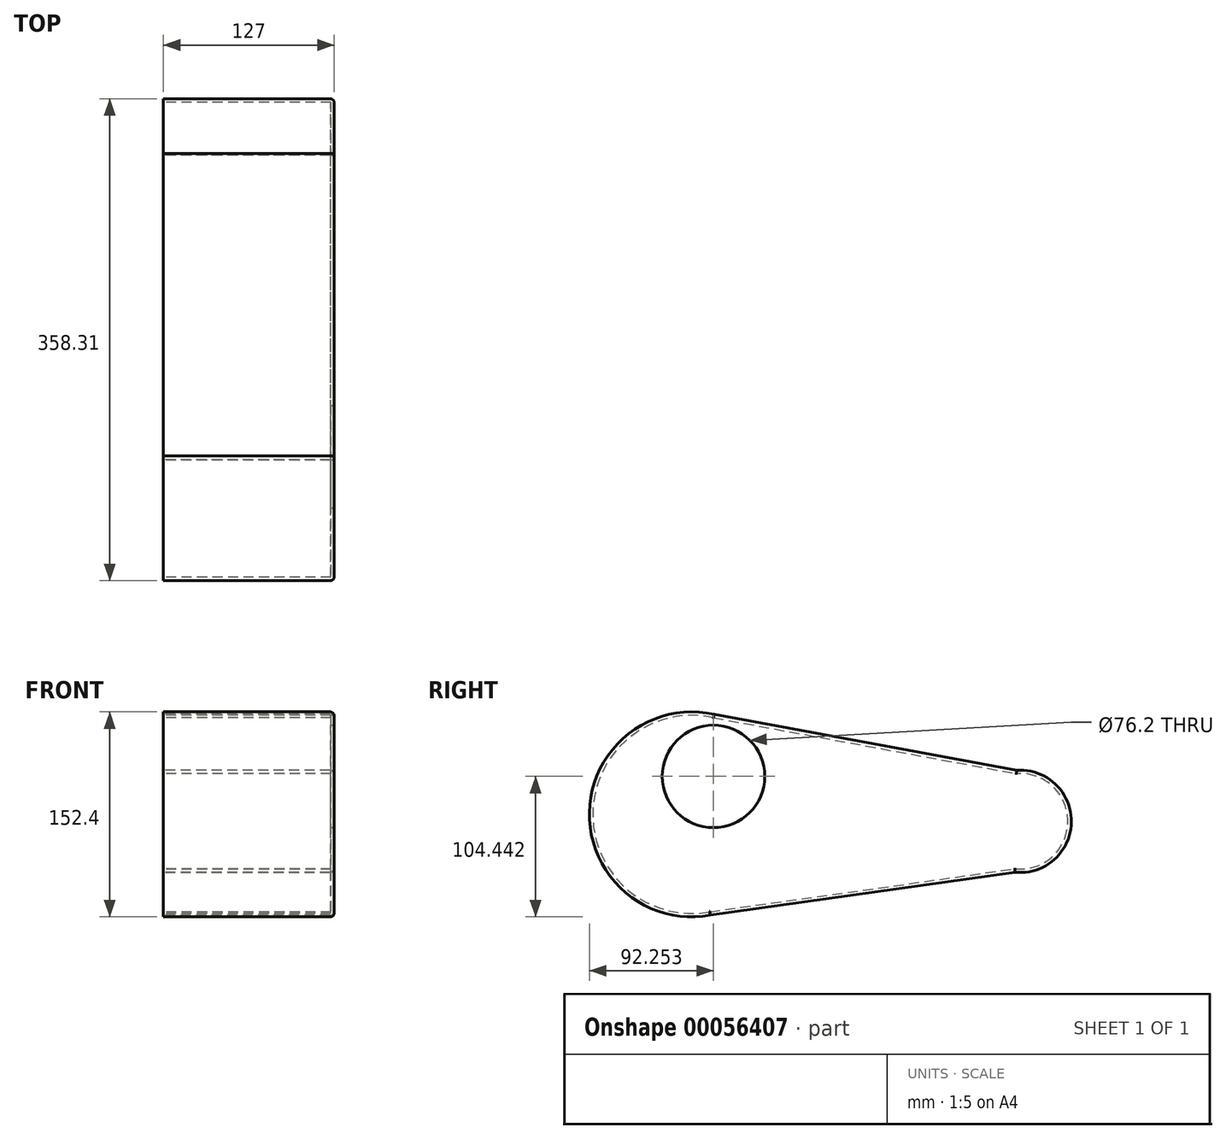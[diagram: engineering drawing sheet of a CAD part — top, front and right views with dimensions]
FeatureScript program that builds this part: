
annotation { "Feature Type Name" : "Feature", "Feature Type Description" : "" }
export const myFeature = defineFeature(function(context is Context, id is Id, definition is map)
    precondition{}
    {
        {
            var Q0;
            Q0=qCreatedBy(makeId("Right.planeOp"),FACE);
            var sketch = newSketch(context, id + "F0", { "sketchPlane" : qUnion([Q0])});
            skCircle(sketch, "E0", {"center": v(0, 0) * mm, "radius": 76.2 * mm});
            skCircle(sketch, "E1", {"center": v(244, -5.13) * mm, "radius": 38.1 * mm});
            skLineSegment(sketch, "E2", {"start": v(16.55, 74.38) * mm, "end": v(241.35, 32.88) * mm});
            skLineSegment(sketch, "E3", {"start": v(13.77, -74.95) * mm, "end": v(240.13, -43.03) * mm});
            skSolve(sketch);
        }
        {
            var Q0;
            {var subQ0=sQuery(id+"F0.wireOp",EDGE,"E0");var subQ1=makeQuery(id+"F0.imprint","INTERSECT",VERTEX,{"derivedFrom":[subQ0,sQuery(id+"F0.wireOp",EDGE,"E2")]});Q0=makeQuery(id+"F0.imprint","IMPRINT",FACE,{"disambiguationData":[TD([[makeQuery(id+"F0.imprint","IMPRINT",EDGE,{"disambiguationData":[TD([[subQ1,-1.0]])],"derivedFrom":subQ0}),1.0]])]});}
            var Q1;
            {var subQ0=sQuery(id+"F0.wireOp",EDGE,"E2");Q1=makeQuery(id+"F0.imprint","IMPRINT",FACE,{"disambiguationData":[TD([[makeQuery(id+"F0.imprint","IMPRINT",EDGE,{"derivedFrom":subQ0}),-1.0]])]});}
            var Q2;
            {var subQ0=sQuery(id+"F0.wireOp",EDGE,"E1");var subQ1=makeQuery(id+"F0.imprint","INTERSECT",VERTEX,{"derivedFrom":[subQ0,sQuery(id+"F0.wireOp",EDGE,"E2")]});Q2=makeQuery(id+"F0.imprint","IMPRINT",FACE,{"disambiguationData":[TD([[makeQuery(id+"F0.imprint","IMPRINT",EDGE,{"disambiguationData":[TD([[subQ1,-1.0]])],"derivedFrom":subQ0}),1.0]])]});}
            extrude(context, id + "F1", {"entities" : qUnion([Q0, Q1, Q2]), "depth" : 127 * mm});
        }
        {
            var Q0;
            Q0=makeQuery(id+"F1.opExtrude","CAP_FACE",FACE,{"disambiguationData":[OSD([sQuery(id+"F0.wireOp",EDGE,"E0"),sQuery(id+"F0.wireOp",EDGE,"E1"),sQuery(id+"F0.wireOp",EDGE,"E2"),sQuery(id+"F0.wireOp",EDGE,"E3")])],"isStart":false});
            var sketch = newSketch(context, id + "F2", { "sketchPlane" : qUnion([Q0])});
            skCircle(sketch, "E4", {"center": v(16.05, 28.24) * mm, "radius": 38.1 * mm});
            skSolve(sketch);
        }
        {
            var Q0;
            Q0=makeQuery(id+"F1.opExtrude","CAP_FACE",FACE,{"disambiguationData":[OSD([sQuery(id+"F0.wireOp",EDGE,"E0"),sQuery(id+"F0.wireOp",EDGE,"E1"),sQuery(id+"F0.wireOp",EDGE,"E2"),sQuery(id+"F0.wireOp",EDGE,"E3")])],"isStart":true});
            shell(context, id + "F3", {"entities" : qUnion([Q0]), "thickness" : 2.54 * mm});
        }
        {
            var Q0;
            Q0=makeQuery(id+"F5.boolean.opBoolean","COPY",EDGE,{"derivedFrom":makeQuery(id+"F5.opExtrude","CAP_EDGE",EDGE,{"disambiguationData":[OSD([sQuery(id+"F2.wireOp",EDGE,"E4")])],"isStart":true})});
            var Q1;
            Q1=makeQuery(id+"F1.opExtrude","CAP_EDGE",EDGE,{"disambiguationData":[OSD([sQuery(id+"F0.wireOp",EDGE,"E2")])],"isStart":false});
            var Q2;
            Q2=makeQuery(id+"F1.opExtrude","CAP_EDGE",EDGE,{"disambiguationData":[OSD([sQuery(id+"F0.wireOp",EDGE,"E0")])],"isStart":false});
            var Q3;
            Q3=makeQuery(id+"F1.opExtrude","CAP_EDGE",EDGE,{"disambiguationData":[OSD([sQuery(id+"F0.wireOp",EDGE,"E1")])],"isStart":false});
            var Q4;
            Q4=makeQuery(id+"F5.boolean.opBoolean","COPY",EDGE,{"derivedFrom":makeQuery(id+"F5.opExtrude","CAP_EDGE",EDGE,{"disambiguationData":[OSD([sQuery(id+"F2.wireOp",EDGE,"E4")])],"isStart":false})});
            fillet(context, id + "F4", {"entities" : qUnion([Q0, Q1, Q2, Q3, Q4]), "radius" : 3.17 * mm, "tangentPropagation" : true, "allowEdgeOverflow" : false});
        }
        {
            var Q0;
            Q0=makeQuery(id+"F2.imprint","IMPRINT",FACE,{"disambiguationData":[TD([[makeQuery(id+"F2.imprint","IMPRINT",EDGE,{"derivedFrom":sQuery(id+"F2.wireOp",EDGE,"E4")}),1.0]])]});
            extrude(context, id + "F5", {"entities" : qUnion([Q0]), "operationType" : NewBodyOperationType.REMOVE, "oppositeDirection" : true, "depth" : 76.2 * mm});
        }
    });
